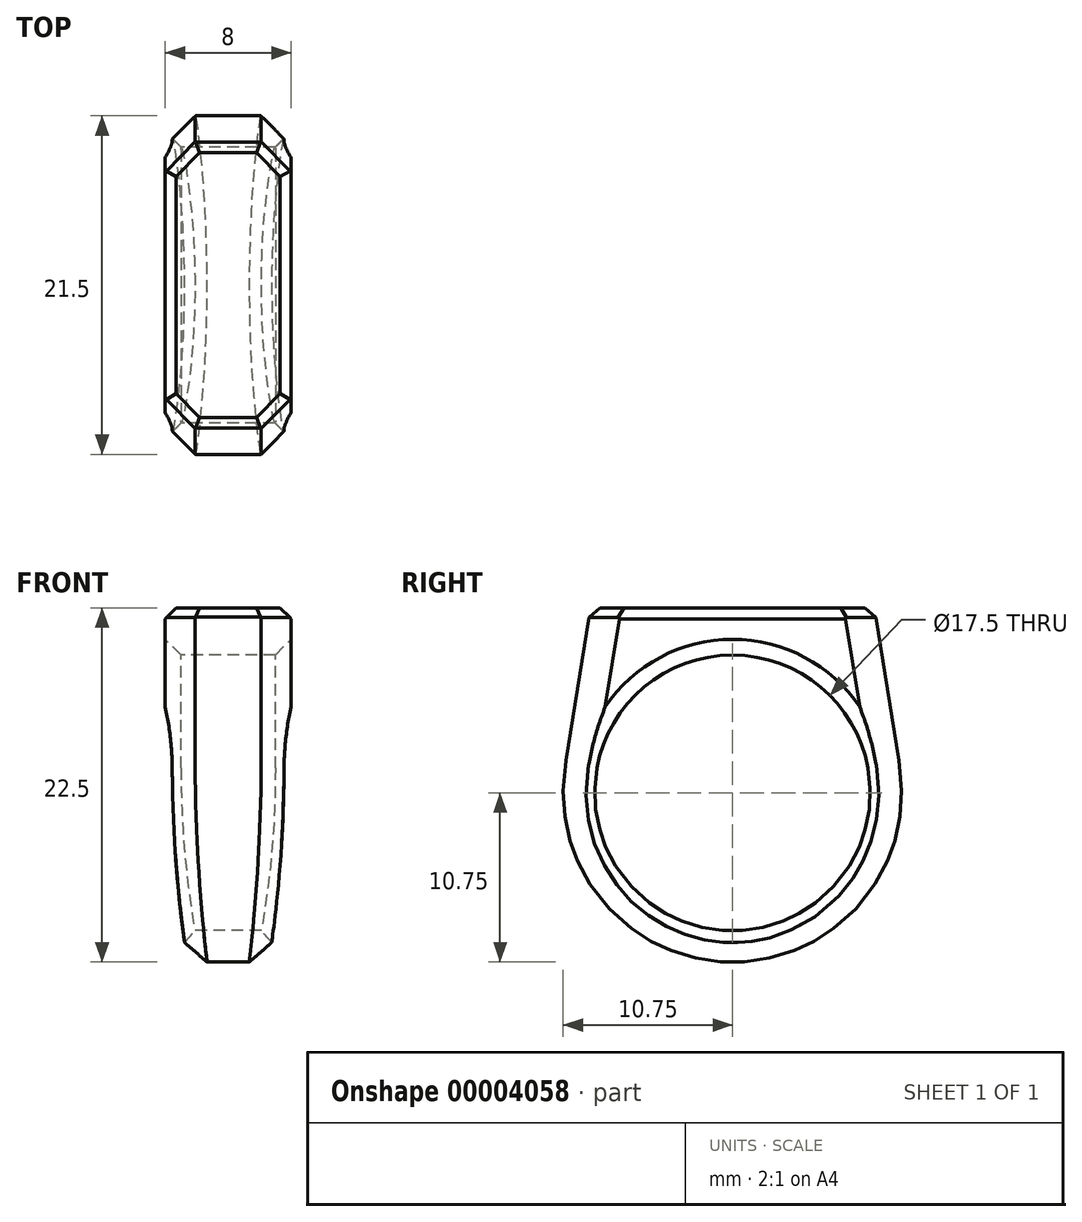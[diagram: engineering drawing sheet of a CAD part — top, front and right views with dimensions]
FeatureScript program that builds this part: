
annotation { "Feature Type Name" : "Feature", "Feature Type Description" : "" }
export const myFeature = defineFeature(function(context is Context, id is Id, definition is map)
    precondition{}
    {
        {
            var Q0;
            Q0=qCreatedBy(makeId("Right.planeOp"),FACE);
            var sketch = newSketch(context, id + "F0", { "sketchPlane" : qUnion([Q0])});
            skCircle(sketch, "E0", {"center": v(0, 0) * mm, "radius": 8.75 * mm});
            skCircle(sketch, "E1", {"center": v(0, 0) * mm, "radius": 10.75 * mm});
            skLineSegment(sketch, "E2", {"start": v(9, 11.75) * mm, "end": v(-9, 11.75) * mm});
            skLineSegment(sketch, "E3", {"start": v(-9, 11.75) * mm, "end": v(-10.61, 1.7) * mm});
            skLineSegment(sketch, "E4", {"start": v(9, 11.75) * mm, "end": v(10.61, 1.7) * mm});
            skPoint(sketch, "E5", {"position": v(0, 11.75) * mm});
            skSolve(sketch);
        }
        {
            var Q0;
            Q0 = qSketchRegion(id + "F0", true);
            extrude(context, id + "F1", {"entities" : qUnion([Q0]), "endBound" : BoundingType.SYMMETRIC, "depth" : 8 * mm});
        }
        {
            var Q0;
            Q0=qCreatedBy(makeId("Front.planeOp"),FACE);
            var sketch = newSketch(context, id + "F2", { "sketchPlane" : qUnion([Q0])});
            skLineSegment(sketch, "E6", {"start": v(4, 1.75) * mm, "end": v(4, 11.75) * mm});
            skLineSegment(sketch, "E7", {"start": v(4, 11.75) * mm, "end": v(9, 11.75) * mm});
            skLineSegment(sketch, "E8", {"start": v(9, 11.75) * mm, "end": v(9, -18.25) * mm});
            skLineSegment(sketch, "E9", {"start": v(9, -18.25) * mm, "end": v(-9, -18.25) * mm});
            skLineSegment(sketch, "E10", {"start": v(-9, -18.25) * mm, "end": v(-9, 11.75) * mm});
            skLineSegment(sketch, "E11", {"start": v(-9, 11.75) * mm, "end": v(-4, 11.75) * mm});
            skLineSegment(sketch, "E12", {"start": v(-4, 11.75) * mm, "end": v(-4, 1.75) * mm});
            skArc(sketch, "E13", {"start": v(2.5, -13.25) * mm, "mid": v(3.62, -5.79) * mm, "end": v(4, 1.75) * mm});
            skArc(sketch, "E14", {"start": v(-4, 1.75) * mm, "mid": v(-3.62, -5.79) * mm, "end": v(-2.5, -13.25) * mm});
            skLineSegment(sketch, "E15", {"start": v(2.5, -13.25) * mm, "end": v(-2.5, -13.25) * mm});
            skPoint(sketch, "E16", {"position": v(0, -13.25) * mm});
            skSolve(sketch);
        }
        {
            var Q0;
            Q0 = qSketchRegion(id + "F2", true);
            extrude(context, id + "F3", {"entities" : qUnion([Q0]), "operationType" : NewBodyOperationType.REMOVE, "endBound" : BoundingType.SYMMETRIC, "oppositeDirection" : true, "depth" : 30 * mm});
        }
        {
            var Q0;
            {var subQ0=sQuery(id+"F0.wireOp",EDGE,"E3");var subQ1=sQuery(id+"F0.wireOp",EDGE,"E2");Q0=makeQuery(id+"F3.boolean.opBoolean","SPLIT",EDGE,{"disambiguationData":[TD([makeQuery(id+"F1.opExtrude","SWEPT_FACE",FACE,{"disambiguationData":[OSD([subQ1])]})])],"derivedFrom":makeQuery(id+"F1.opExtrude","CAP_EDGE",EDGE,{"disambiguationData":[OSD([subQ0])],"isStart":true})});}
            var Q1;
            {var subQ0=sQuery(id+"F0.wireOp",EDGE,"E4");var subQ1=sQuery(id+"F0.wireOp",EDGE,"E2");Q1=makeQuery(id+"F3.boolean.opBoolean","SPLIT",EDGE,{"disambiguationData":[TD([makeQuery(id+"F1.opExtrude","SWEPT_FACE",FACE,{"disambiguationData":[OSD([subQ1])]})])],"derivedFrom":makeQuery(id+"F1.opExtrude","CAP_EDGE",EDGE,{"disambiguationData":[OSD([subQ0])],"isStart":false})});}
            chamfer(context, id + "F4", {"entities" : qUnion([Q0, Q1]), "width" : 1.9 * mm, "tangentPropagation" : true});
        }
        {
            var Q0;
            Q0=makeQuery(id+"F1.opExtrude","CAP_EDGE",EDGE,{"disambiguationData":[OSD([sQuery(id+"F0.wireOp",EDGE,"E0")])],"isStart":true});
            var Q1;
            Q1=makeQuery(id+"F1.opExtrude","CAP_EDGE",EDGE,{"disambiguationData":[OSD([sQuery(id+"F0.wireOp",EDGE,"E0")])],"isStart":false});
            chamfer(context, id + "F5", {"entities" : qUnion([Q0, Q1]), "width" : 1 * mm, "tangentPropagation" : true});
        }
        {
            var Q0;
            Q0=makeQuery(id+"F1.opExtrude","CAP_EDGE",EDGE,{"disambiguationData":[OSD([sQuery(id+"F0.wireOp",EDGE,"E2")])],"isStart":true});
            var Q1;
            {var subQ0=sQuery(id+"F0.wireOp",EDGE,"E4");var subQ1=sQuery(id+"F0.wireOp",EDGE,"E2");var subQ2=makeQuery(id+"F1.opExtrude","SWEPT_FACE",FACE,{"disambiguationData":[OSD([subQ1])]});Q1=makeQuery(id+"F4.opChamfer","BLEND_EDGE",EDGE,{"blendedFrom":[makeQuery(id+"F3.boolean.opBoolean","SPLIT",EDGE,{"disambiguationData":[TD([subQ2])],"derivedFrom":makeQuery(id+"F1.opExtrude","CAP_EDGE",EDGE,{"disambiguationData":[OSD([subQ0])],"isStart":true})}),subQ2],"blendedInto":[subQ2]});}
            var Q2;
            Q2=makeQuery(id+"F1.opExtrude","SWEPT_EDGE",EDGE,{"disambiguationData":[OSD([sQuery(id+"F0.wireOp",EDGE,"E2"),sQuery(id+"F0.wireOp",EDGE,"E4")])]});
            var Q3;
            {var subQ0=sQuery(id+"F0.wireOp",EDGE,"E4");var subQ1=sQuery(id+"F0.wireOp",EDGE,"E2");var subQ2=makeQuery(id+"F1.opExtrude","SWEPT_FACE",FACE,{"disambiguationData":[OSD([subQ1])]});Q3=makeQuery(id+"F4.opChamfer","BLEND_EDGE",EDGE,{"blendedFrom":[makeQuery(id+"F3.boolean.opBoolean","SPLIT",EDGE,{"disambiguationData":[TD([subQ2])],"derivedFrom":makeQuery(id+"F1.opExtrude","CAP_EDGE",EDGE,{"disambiguationData":[OSD([subQ0])],"isStart":false})}),subQ2],"blendedInto":[subQ2]});}
            var Q4;
            Q4=makeQuery(id+"F1.opExtrude","CAP_EDGE",EDGE,{"disambiguationData":[OSD([sQuery(id+"F0.wireOp",EDGE,"E2")])],"isStart":false});
            var Q5;
            {var subQ0=sQuery(id+"F0.wireOp",EDGE,"E3");var subQ1=sQuery(id+"F0.wireOp",EDGE,"E2");var subQ2=makeQuery(id+"F1.opExtrude","SWEPT_FACE",FACE,{"disambiguationData":[OSD([subQ1])]});Q5=makeQuery(id+"F4.opChamfer","BLEND_EDGE",EDGE,{"blendedFrom":[makeQuery(id+"F3.boolean.opBoolean","SPLIT",EDGE,{"disambiguationData":[TD([subQ2])],"derivedFrom":makeQuery(id+"F1.opExtrude","CAP_EDGE",EDGE,{"disambiguationData":[OSD([subQ0])],"isStart":false})}),subQ2],"blendedInto":[subQ2]});}
            var Q6;
            Q6=makeQuery(id+"F1.opExtrude","SWEPT_EDGE",EDGE,{"disambiguationData":[OSD([sQuery(id+"F0.wireOp",EDGE,"E2"),sQuery(id+"F0.wireOp",EDGE,"E3")])]});
            var Q7;
            {var subQ0=sQuery(id+"F0.wireOp",EDGE,"E3");var subQ1=sQuery(id+"F0.wireOp",EDGE,"E2");var subQ2=makeQuery(id+"F1.opExtrude","SWEPT_FACE",FACE,{"disambiguationData":[OSD([subQ1])]});Q7=makeQuery(id+"F4.opChamfer","BLEND_EDGE",EDGE,{"blendedFrom":[makeQuery(id+"F3.boolean.opBoolean","SPLIT",EDGE,{"disambiguationData":[TD([subQ2])],"derivedFrom":makeQuery(id+"F1.opExtrude","CAP_EDGE",EDGE,{"disambiguationData":[OSD([subQ0])],"isStart":true})}),subQ2],"blendedInto":[subQ2]});}
            chamfer(context, id + "F6", {"entities" : qUnion([Q0, Q1, Q2, Q3, Q4, Q5, Q6, Q7]), "width" : 0.7 * mm, "tangentPropagation" : true});
        }
    });
